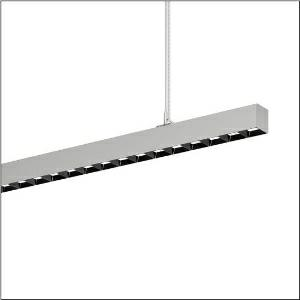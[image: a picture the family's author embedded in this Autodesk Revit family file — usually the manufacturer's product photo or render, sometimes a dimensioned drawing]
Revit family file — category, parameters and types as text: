
# Revit family: silica_r__21_51mx32dr3fsb_c6eb
name_source: partatom
category: Lighting Fixtures
units: mm (PartAtom-declared; Revit-internal decimal feet)

## family parameters
Cut with Voids When Loaded = No
Host = Face
Light Source = No
Part Type = Normal
Room Calculation Point = No
Round Connector Dimension = Use Diameter
Shared = No

## types (1)
- --- (1 x LED, 21860 lm, 137.9 W, 3000K)
    Apparent Load = 138 VA
    CIE Flux Codes = 86 99 100 59 100
    Color Rendering = 80
    Color Temperature = 3000K
    Default Elevation = 1800 mm
    Description = Silica® 21, office luminaire, primary light control with darklight reflector, of PMMA, black, CAT 2 (L<= 3000cd/m²), light emission: direct/indirect distribution, primary light characteristic: symmetric, installation type: suspended mounting, LED, rated luminous flux: 21.860lm, luminous efficacy: 159lm/W, light colour: 830, colour temperature: 3000K, control gear: DALI 2, with terminal, 3+2-pole, max. 2.5mm², mains connection: 220..240V, AC, 50/60Hz, rated input power: 137.9W, luminaire housing, of aluminium, metallic grey (RAL 9006), length: 3.604mm, width: 53mm, height: 53mm, protection rating (complete): IP20, insulation class (complete): insulation class I (protective earthing), certification: CE, permissible operating ambient temperature: 0..+35°C, standard: EN 50419, packaging unit: 1 piece
    Height = 53 mm
    Lamp = 1 x LED
    Lamp Light Flux = 21860 lm
    Lamp Power = 137.9 W
    Lamp count = 1
    Length = 3604 mm
    Luminous efficacy = 159 lm/W
    Manufacturer = Siteco
    ModVariant = No
    Model = 51MX32DR3FSB
    Mounting Place = Ceiling
    Mounting Type = Pendant
    Number of Poles = 1
    OnlyDefault = Yes
    Power Factor = 1
    Product Name = Silica® 21
    Product group = office luminaire | ceiling pendant
    ProductGroupID = 903
    Protection Class = Protection class I
    Protection Degree = IP 20
    RLX_Detail_Level = 1
    RLX_Emergency_Light_Flux = 0 lm
    RLX_Emergency_Type = 0
    RLX_Emergency_Type_DB = No
    RlxData = <blob elided: 38689 chars, md5=a7b24a42>
    Socket = socket
    Standby Power = 0 W
    System Light Flux = 21860 lm
    System Power = 138 W
    Type Comments = factory setting: luminous flux: 100 % | dim-lin: 254 | 391 mA
    Type Image = l_1335859.jpg
    URL = http://relux.com
    VarID = @adj_054589
    Voltage = 0 V
    Weight = 0.00 kg
    Width = 53 mm

## geometry (parser evidence)
native form markers: Blend x4, Sweep x12
no freeform markers — native parametric forms only
